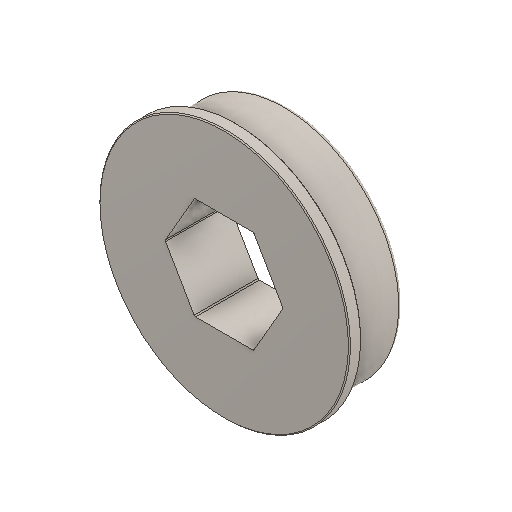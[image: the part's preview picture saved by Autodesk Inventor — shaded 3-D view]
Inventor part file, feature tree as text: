
AUTODESK INVENTOR PART (.ipt)
format: ipt  version: 2024.1 (Build 281209000, 209)  size: 155,136 bytes
history: native  units: in
note: dims shown in document units (in); Inventor stores cm internally (conversion verified against a paired STEP export)
features: fillet x1
ambient origin geometry x8: Origin, YZ Plane, XZ Plane, XY Plane, X Axis, Y Axis, Z Axis, Center Point
bodies: Solid1 (feature_tree)
feature tree (1):
  fillet  "Fillet2"  [1 undecoded]
note: 1 required parameter value undecoded (feature->parameter linkage not recoverable at this tier; creation-order binding heuristic only, values carry confidence <= 0.55)
